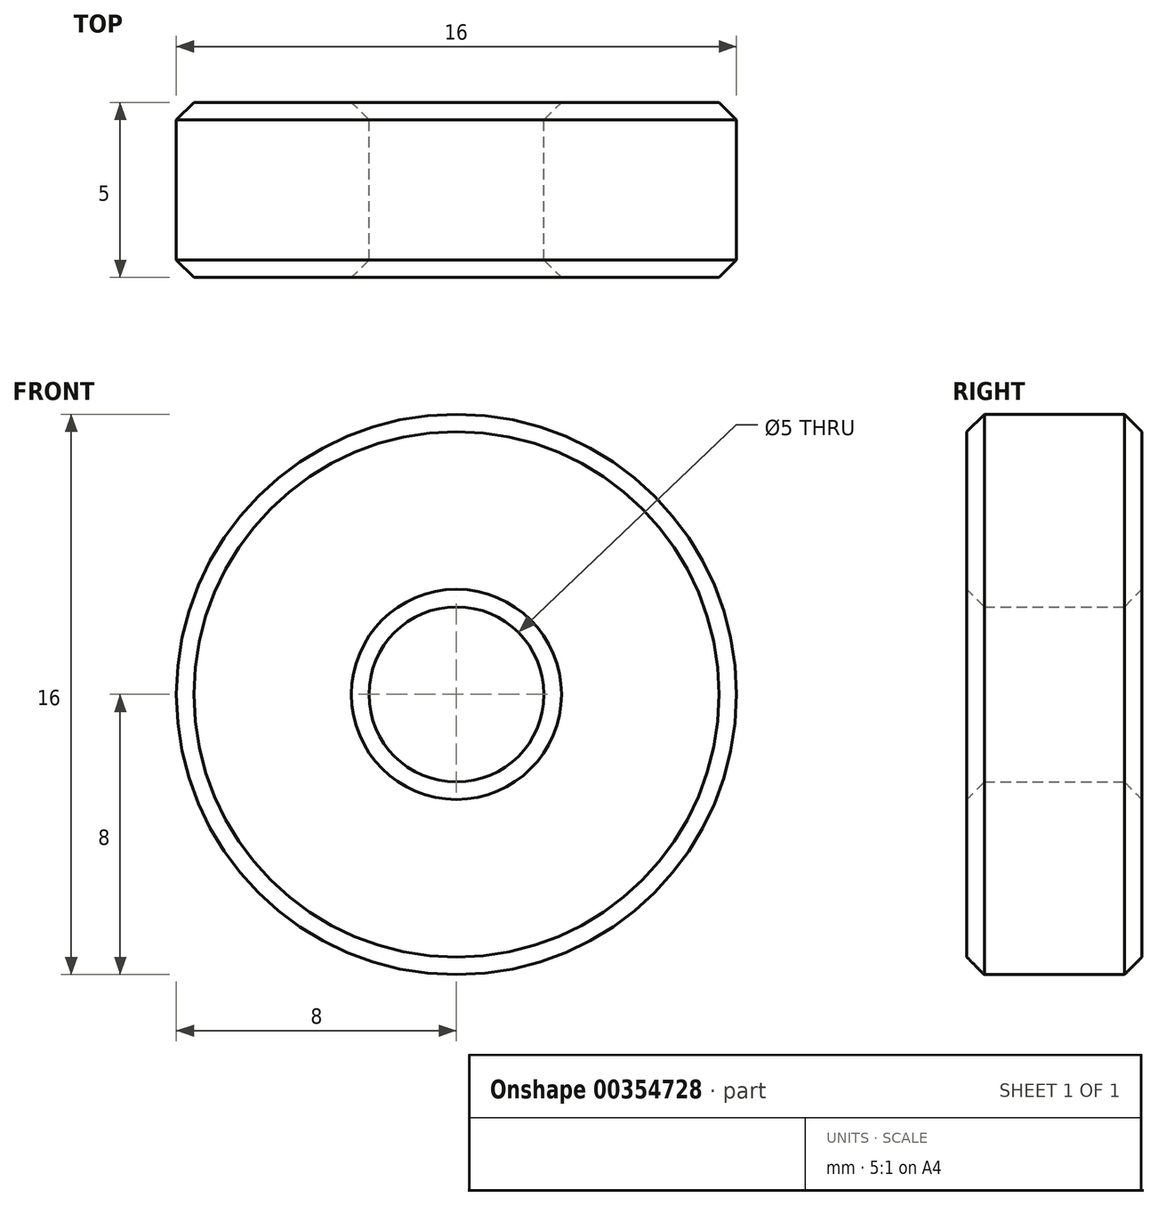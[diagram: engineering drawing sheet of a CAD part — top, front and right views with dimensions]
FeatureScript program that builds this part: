
annotation { "Feature Type Name" : "Feature", "Feature Type Description" : "" }
export const myFeature = defineFeature(function(context is Context, id is Id, definition is map)
    precondition{}
    {
        {
            var Q0;
            Q0=qCreatedBy(makeId("Front.planeOp"),FACE);
            var sketch = newSketch(context, id + "F0", { "sketchPlane" : qUnion([Q0])});
            skCircle(sketch, "E0", {"center": v(0, 0) * mm, "radius": 8 * mm});
            skCircle(sketch, "E1", {"center": v(0, 0) * mm, "radius": 2.5 * mm});
            skSolve(sketch);
        }
        {
            var Q0;
            Q0=qSketchRegion(id+"F0",true);
            extrude(context, id + "F1", {"entities" : qUnion([Q0]), "depth" : 5 * mm});
        }
        {
            var Q0;
            Q0=makeQuery(id+"F1.opExtrude","CAP_EDGE",EDGE,{"disambiguationData":[OSD([sQuery(id+"F0.wireOp",EDGE,"E0")])],"isStart":false});
            var Q1;
            Q1=makeQuery(id+"F1.opExtrude","CAP_EDGE",EDGE,{"disambiguationData":[OSD([sQuery(id+"F0.wireOp",EDGE,"E0")])],"isStart":true});
            var Q2;
            Q2=makeQuery(id+"F1.opExtrude","CAP_EDGE",EDGE,{"disambiguationData":[OSD([sQuery(id+"F0.wireOp",EDGE,"E1")])],"isStart":true});
            var Q3;
            Q3=makeQuery(id+"F1.opExtrude","CAP_EDGE",EDGE,{"disambiguationData":[OSD([sQuery(id+"F0.wireOp",EDGE,"E1")])],"isStart":false});
            chamfer(context, id + "F2", {"entities" : qUnion([Q0, Q1, Q2, Q3]), "width" : .5 * mm, "tangentPropagation" : true});
        }
    });
